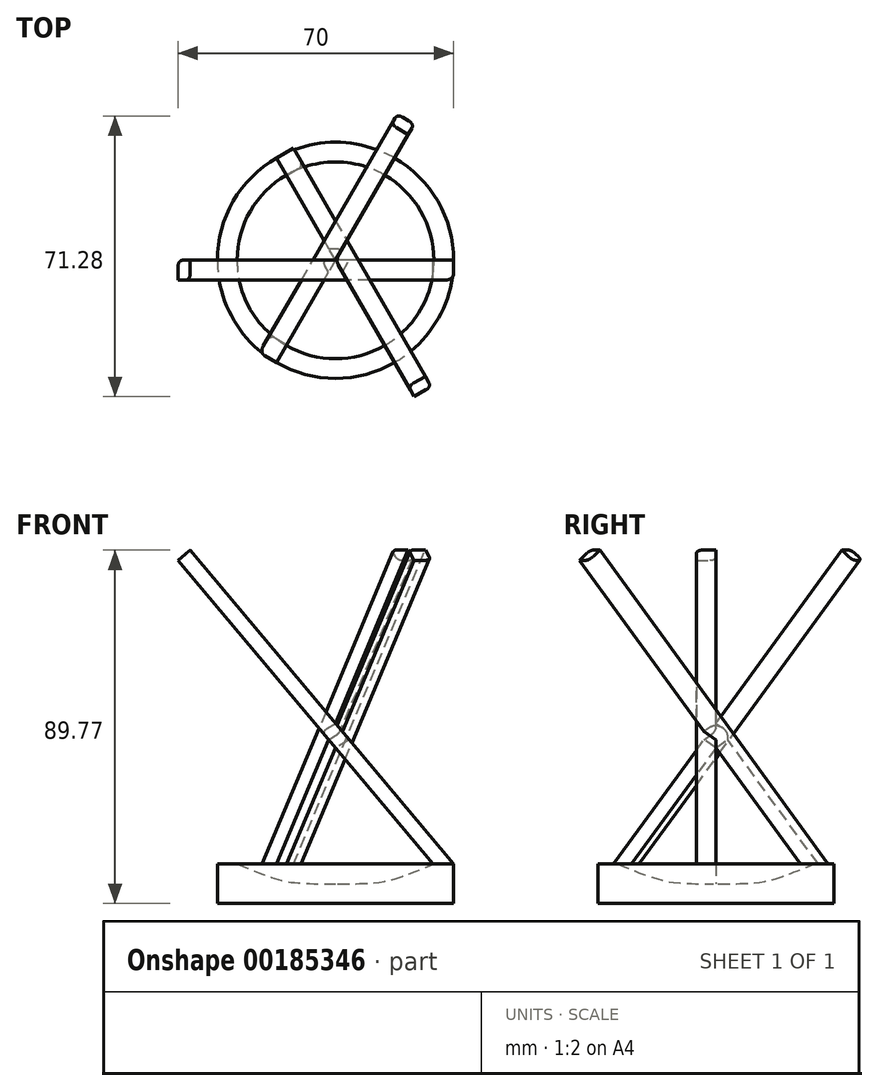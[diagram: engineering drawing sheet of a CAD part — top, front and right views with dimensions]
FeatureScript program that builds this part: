
annotation { "Feature Type Name" : "Feature", "Feature Type Description" : "" }
export const myFeature = defineFeature(function(context is Context, id is Id, definition is map)
    precondition{}
    {
        {
            var Q0;
            Q0=qCreatedBy(makeId("Front.planeOp"),FACE);
            var sketch = newSketch(context, id + "F0", { "sketchPlane" : qUnion([Q0])});
            skLineSegment(sketch, "E0", {"start": v(-25, 0) * mm, "end": v(0, 0) * mm});
            skLineSegment(sketch, "E1", {"start": v(-25, 0) * mm, "end": v(-25, 10) * mm});
            skPoint(sketch, "E2", {"position": v(0, 0) * mm});
            skLineSegment(sketch, "E3", {"start": v(0, 5) * mm, "end": v(0, 0) * mm});
            skLineSegment(sketch, "E4", {"start": v(-25, 10) * mm, "end": v(-30, 10) * mm});
            skLineSegment(sketch, "E5", {"start": v(-30, 10) * mm, "end": v(-30, 0) * mm});
            skLineSegment(sketch, "E6", {"start": v(-30, 0) * mm, "end": v(-25, 0) * mm});
            skFitSpline(sketch, "E7", {"points": [v(-25, 10) * mm, v(0, 5) * mm], "startDerivative": vector(37.5, -15) * mm, "endDerivative": vector(37.5, 0) * mm});
            skPoint(sketch, "E8", {"position": v(-12.5, 0) * mm});
            skSolve(sketch);
        }
        {
            var Q0;
            Q0=makeQuery(id+"F0.imprint","IMPRINT",FACE,{"disambiguationData":[TD([[makeQuery(id+"F0.imprint","IMPRINT",EDGE,{"derivedFrom":sQuery(id+"F0.wireOp",EDGE,"E1")}),1.0]])]});
            var Q1;
            Q1=makeQuery(id+"F0.imprint","IMPRINT",FACE,{"disambiguationData":[TD([[makeQuery(id+"F0.imprint","IMPRINT",EDGE,{"derivedFrom":sQuery(id+"F0.wireOp",EDGE,"E0")}),1.0]])]});
            var Q2;
            Q2=sQuery(id+"F0.wireOp",EDGE,"E3");
            revolve(context, id + "F1", {"entities" : qUnion([Q0, Q1]), "axis" : qUnion([Q2]), "revolveType" : RevolveType.FULL});
        }
        {
            var Q0;
            Q0=qCreatedBy(makeId("Front.planeOp"),FACE);
            var sketch = newSketch(context, id + "F2", { "sketchPlane" : qUnion([Q0])});
            skLineSegment(sketch, "E9", {"start": v(30, 10) * mm, "end": v(-36.94, 89.77) * mm});
            skLineSegment(sketch, "E10", {"start": v(-36.94, 89.77) * mm, "end": v(-40, 87.2) * mm});
            skLineSegment(sketch, "E11", {"start": v(-40, 87.2) * mm, "end": v(24.78, 10) * mm});
            skLineSegment(sketch, "E12", {"start": v(24.78, 10) * mm, "end": v(30, 10) * mm});
            skLineSegment(sketch, "E13.0", {"start": v(-30, 10) * mm, "end": v(30, 10) * mm});
            skLineSegment(sketch, "E14", {"start": v(-30, 10) * mm, "end": v(-30, 91.77) * mm, "construction": true});
            skSolve(sketch);
        }
        {
            var Q0;
            Q0 = qSketchRegion(id + "F2", true);
            extrude(context, id + "F3", {"entities" : qUnion([Q0]), "operationType" : NewBodyOperationType.ADD, "depth" : 5 * mm, "offsetDistance" : 25 * mm});
        }
        {
            var Q0;
            Q0=makeQuery(id+"F1.opRevolve","SWEPT_BODY",BODY,{"disambiguationData":[OSD([sQuery(id+"F0.wireOp",EDGE,"E0"),sQuery(id+"F0.wireOp",EDGE,"E3"),sQuery(id+"F0.wireOp",EDGE,"E4"),sQuery(id+"F0.wireOp",EDGE,"E5"),sQuery(id+"F0.wireOp",EDGE,"E6"),sQuery(id+"F0.wireOp",EDGE,"E7")])]});
            var Q1;
            Q1=sQuery(id+"F0.wireOp",EDGE,"E3");
            circularPattern(context, id + "F4", {"operationType" : NewBodyOperationType.ADD, "entities" : qUnion([Q0]), "axis" : qUnion([Q1]), "angle" : 360 * degree, "instanceCount" : 3, "equalSpace" : true});
        }
        {
            var Q0;
            {var subQ1=sQuery(id+"F2.wireOp",EDGE,"E9");var subQ3=makeQuery(id+"F3.opExtrude","SWEPT_FACE",FACE,{"disambiguationData":[OSD([subQ1])]});Q0=makeQuery(id+"F4.boolean.opBoolean","SPLIT",EDGE,{"disambiguationData":[TD([subQ3])],"derivedFrom":makeQuery(id+"F4.opPattern","COPY",EDGE,{"derivedFrom":makeQuery(id+"F3.opExtrude","CAP_EDGE",EDGE,{"disambiguationData":[OSD([subQ1])],"isStart":true}),"instanceName":"2"})});}
            var Q1;
            Q1=makeQuery(id+"F4.opPattern","COPY",EDGE,{"derivedFrom":makeQuery(id+"F3.opExtrude","CAP_EDGE",EDGE,{"disambiguationData":[OSD([sQuery(id+"F2.wireOp",EDGE,"E11")])],"isStart":false}),"instanceName":"2"});
            var Q2;
            Q2=makeQuery(id+"F3.opExtrude","CAP_EDGE",EDGE,{"disambiguationData":[OSD([sQuery(id+"F2.wireOp",EDGE,"E9")])],"isStart":false});
            var Q3;
            Q3=makeQuery(id+"F4.opPattern","COPY",EDGE,{"derivedFrom":makeQuery(id+"F3.opExtrude","CAP_EDGE",EDGE,{"disambiguationData":[OSD([sQuery(id+"F2.wireOp",EDGE,"E9")])],"isStart":false}),"instanceName":"1"});
            var Q4;
            {var subQ0=sQuery(id+"F2.wireOp",EDGE,"E11");var subQ1=sQuery(id+"F2.wireOp",EDGE,"E10");Q4=makeQuery(id+"F4.boolean.opBoolean","SPLIT",EDGE,{"disambiguationData":[TD([makeQuery(id+"F3.opExtrude","SWEPT_FACE",FACE,{"disambiguationData":[OSD([subQ1])]})])],"derivedFrom":makeQuery(id+"F3.opExtrude","CAP_EDGE",EDGE,{"disambiguationData":[OSD([subQ0])],"isStart":true})});}
            var Q5;
            {var subQ0=sQuery(id+"F2.wireOp",EDGE,"E11");var subQ1=sQuery(id+"F2.wireOp",EDGE,"E10");Q5=makeQuery(id+"F4.boolean.opBoolean","SPLIT",EDGE,{"disambiguationData":[TD([makeQuery(id+"F4.opPattern","COPY",FACE,{"derivedFrom":makeQuery(id+"F3.opExtrude","SWEPT_FACE",FACE,{"disambiguationData":[OSD([subQ1])]}),"instanceName":"1"})])],"derivedFrom":makeQuery(id+"F4.opPattern","COPY",EDGE,{"derivedFrom":makeQuery(id+"F3.opExtrude","CAP_EDGE",EDGE,{"disambiguationData":[OSD([subQ0])],"isStart":true}),"instanceName":"1"})});}
            var Q6;
            Q6=makeQuery(id+"F4.opPattern","COPY",EDGE,{"derivedFrom":makeQuery(id+"F3.opExtrude","CAP_EDGE",EDGE,{"disambiguationData":[OSD([sQuery(id+"F2.wireOp",EDGE,"E11")])],"isStart":false}),"instanceName":"1"});
            fillet(context, id + "F5", {"entities" : qUnion([Q0, Q1, Q2, Q3, Q4, Q5, Q6]), "radius" : 1.5 * mm, "tangentPropagation" : true, "allowEdgeOverflow" : false});
        }
    });
